# Revit family: Studio 3D Soundproof Interior Doors
name_source: partatom
category: Doors
units: mm (PartAtom-declared; Revit-internal decimal feet)

## family parameters
Always vertical = Yes
Cut with Voids When Loaded = No
Host = Wall
OmniClass Number = 23.30.10.00
OmniClass Title = Doors
Room Calculation Point = No
Shared = No

## types (3) — shared parameters
1. Satin Chrome (Standard) = Yes
1. Venice (Standard) = Yes
2. Allegro = No
2. Polished Chrome = No
3. Polished Brass = No
3. Torino = No
4. Customer Supplied Handle = No
4. Oil Rubbed Bronze = No
5. Dark Bronze Powder Coat = No
6. Satin nickel = No
7. Dark Bronze Anodized = No
8. Pewter or Antique Nickel = No
9. Black = No
Analytic Construction = <None>
Assembly Code = C1020
Define Thermal Properties by = Schematic Type
Description = Studio 3 Soundproof Interior Doors
Finish = Ready to Stain
Function = Interior
Handle Finish = 1
Handle Option = 1
Height = 7' - 1"
Jamb Material = Studio 3D Soundproof Door
Manufacturer = Acoustical Surfaces, Inc.
Panel Material = Studio 3D Soundproof Door
Rough Height = 7' - 1"
Rough Width = 3' - 1 1/2"
Type Comments = Soundproof Interior Doors
URL = https://www.acousticalsurfaces.com
Wall Closure = By host
Width = 3' - 1 1/2"

## per-type parameters (varying)
| type | 0. Standard | 1. 6 inch Extension | 2. 12 inch Extension | JE | Jamb Extension Option |
| 12 inch Jamb | No | No | Yes | 1' - 6" | 2 |
| 6 inch Jamb | No | Yes | No | 1' - 0" | 1 |
| Standard | Yes | No | No | 0' - 6" | 0 |

## geometry (parser evidence)
native form markers: Sweep x7
no freeform markers — native parametric forms only
